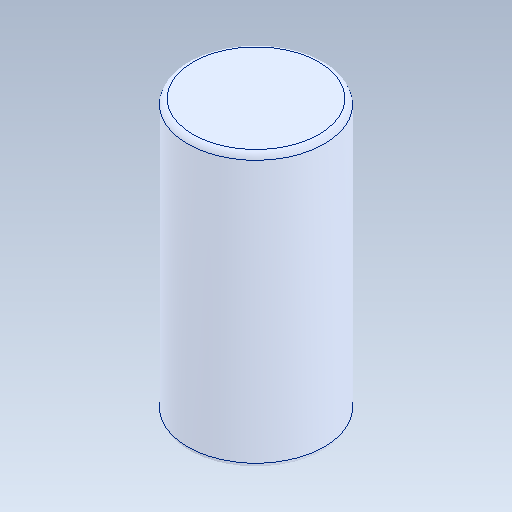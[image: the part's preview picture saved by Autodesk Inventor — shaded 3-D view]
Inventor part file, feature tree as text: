
AUTODESK INVENTOR PART (.ipt)
format: ipt  version: 2020 (Build 240168000, 168)  size: 100,352 bytes
history: native  units: in
note: dims shown in document units (in); Inventor stores cm internally (conversion verified against a paired STEP export)
features: fillet x1
ambient origin geometry x8: Origin, YZ Plane, XZ Plane, XY Plane, X Axis, Y Axis, Z Axis, Center Point
bodies: Solid1 (feature_tree)
feature tree (1):
  fillet  "Fillet1"  [1 undecoded]
note: 1 required parameter value undecoded (feature->parameter linkage not recoverable at this tier; creation-order binding heuristic only, values carry confidence <= 0.55)
